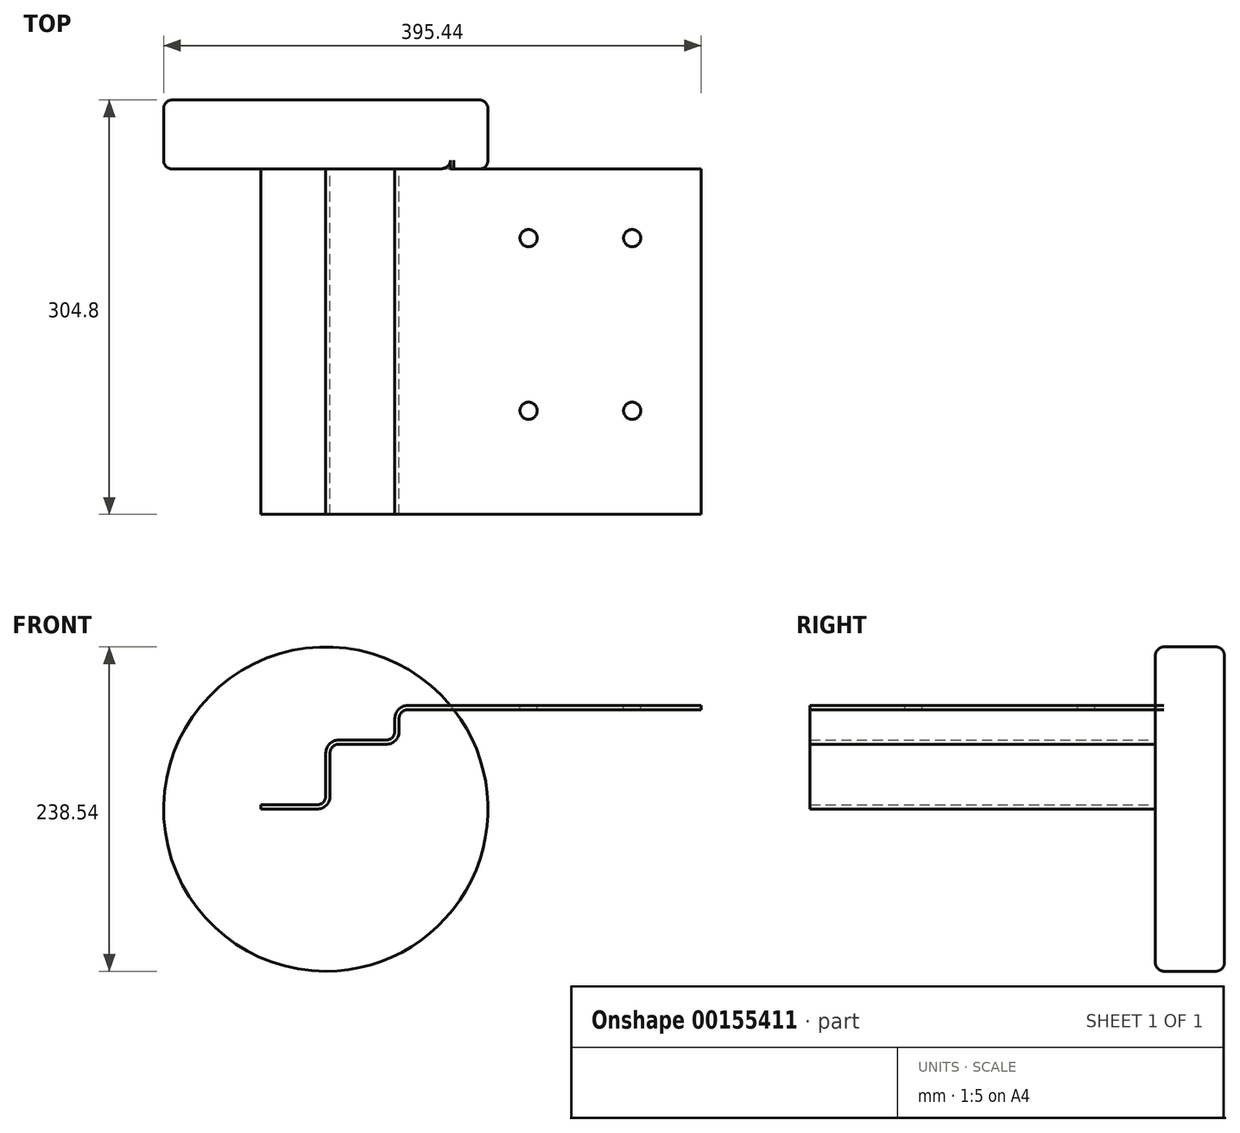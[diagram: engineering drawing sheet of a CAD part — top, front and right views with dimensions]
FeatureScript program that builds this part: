
annotation { "Feature Type Name" : "Feature", "Feature Type Description" : "" }
export const myFeature = defineFeature(function(context is Context, id is Id, definition is map)
    precondition{}
    {
        {
            var Q0;
            Q0=qCreatedBy(makeId("Front.planeOp"),FACE);
            var sketch = newSketch(context, id + "F0", { "sketchPlane" : qUnion([Q0])});
            skLineSegment(sketch, "E0", {"start": v(0, 9.53) * mm, "end": v(0, 41.28) * mm});
            skLineSegment(sketch, "E1", {"start": v(9.52, 50.8) * mm, "end": v(44.45, 50.8) * mm});
            skLineSegment(sketch, "E2", {"start": v(50.8, 57.15) * mm, "end": v(50.8, 66.68) * mm});
            skLineSegment(sketch, "E3", {"start": v(60.33, 76.2) * mm, "end": v(276.17, 76.2) * mm});
            skLineSegment(sketch, "E4.0", {"start": v(60.33, 73.03) * mm, "end": v(276.17, 73.03) * mm});
            skLineSegment(sketch, "E5.0", {"start": v(53.98, 57.15) * mm, "end": v(53.98, 66.68) * mm});
            skLineSegment(sketch, "E6.0", {"start": v(3.18, 9.53) * mm, "end": v(3.18, 41.28) * mm});
            skLineSegment(sketch, "E7", {"start": v(9.52, 47.63) * mm, "end": v(44.45, 47.63) * mm});
            skPoint(sketch, "E8.visualSharp", {"position": v(53.98, 73.03) * mm});
            skArc(sketch, "E8.filletArc", {"start": v(60.33, 73.03) * mm, "mid": v(55.83, 71.17) * mm, "end": v(53.97, 66.68) * mm});
            skArc(sketch, "E9.0", {"start": v(60.33, 76.2) * mm, "mid": v(53.59, 73.41) * mm, "end": v(50.8, 66.68) * mm});
            skPoint(sketch, "E10.visualSharp", {"position": v(50.8, 50.8) * mm});
            skArc(sketch, "E10.filletArc", {"start": v(44.45, 50.8) * mm, "mid": v(48.94, 52.66) * mm, "end": v(50.8, 57.15) * mm});
            skPoint(sketch, "E11.visualSharp", {"position": v(3.18, 47.63) * mm});
            skArc(sketch, "E11.filletArc", {"start": v(9.52, 47.63) * mm, "mid": v(5.03, 45.77) * mm, "end": v(3.17, 41.28) * mm});
            skArc(sketch, "E12.0", {"start": v(44.45, 47.63) * mm, "mid": v(51.19, 50.41) * mm, "end": v(53.98, 57.15) * mm});
            skArc(sketch, "E13.0", {"start": v(9.52, 50.8) * mm, "mid": v(2.79, 48.01) * mm, "end": v(0, 41.28) * mm});
            skPoint(sketch, "E14.orphan", {"position": v(0, 50.8) * mm});
            skLineSegment(sketch, "E15", {"start": v(-47.63, 3.17) * mm, "end": v(-6.35, 3.18) * mm});
            skPoint(sketch, "E16.orphan", {"position": v(0, 0) * mm});
            skLineSegment(sketch, "E17", {"start": v(-47.63, 0) * mm, "end": v(-47.63, 3.17) * mm});
            skPoint(sketch, "E18.visualSharp", {"position": v(0, 3.18) * mm});
            skArc(sketch, "E18.filletArc", {"start": v(-6.35, 3.18) * mm, "mid": v(-1.86, 5.03) * mm, "end": v(0, 9.53) * mm});
            skArc(sketch, "E19.0", {"start": v(-6.35, 0) * mm, "mid": v(0.39, 2.79) * mm, "end": v(3.18, 9.53) * mm});
            skLineSegment(sketch, "E20.trimOffspring", {"start": v(-6.35, 0) * mm, "end": v(-47.63, 0) * mm});
            skLineSegment(sketch, "E21", {"start": v(276.17, 73.03) * mm, "end": v(276.17, 76.2) * mm});
            skSolve(sketch);
        }
        {
            var Q0;
            Q0=makeQuery(id+"F0.imprint","IMPRINT",FACE,{"disambiguationData":[TD([[makeQuery(id+"F0.imprint","IMPRINT",EDGE,{"derivedFrom":sQuery(id+"F0.wireOp",EDGE,"E0")}),-1.0]])]});
            extrude(context, id + "F1", {"entities" : qUnion([Q0]), "depth" : 254 * mm});
        }
        {
            var Q0;
            Q0=qCreatedBy(makeId("Front.planeOp"),FACE);
            var sketch = newSketch(context, id + "F2", { "sketchPlane" : qUnion([Q0])});
            skCircle(sketch, "E22", {"center": v(0, 0) * mm, "radius": 119.27 * mm});
            skSolve(sketch);
        }
        {
            var Q0;
            Q0=makeQuery(id+"F2.imprint","IMPRINT",FACE,{"disambiguationData":[TD([[makeQuery(id+"F2.imprint","IMPRINT",EDGE,{"derivedFrom":sQuery(id+"F2.wireOp",EDGE,"E22")}),1.0]])]});
            extrude(context, id + "F3", {"entities" : qUnion([Q0]), "operationType" : NewBodyOperationType.ADD, "oppositeDirection" : true, "depth" : 50.8 * mm});
        }
        {
            var Q0;
            {var subQ0=sQuery(id+"F2.wireOp",EDGE,"E22");Q0=makeQuery(id+"F3.boolean.opBoolean","SPLIT",EDGE,{"disambiguationData":[topologyDisambiguationEdgeConnected([makeQuery(id+"F3.opExtrude","CAP_FACE",FACE,{"disambiguationData":[OSD([subQ0])],"isStart":true})])],"derivedFrom":makeQuery(id+"F3.opExtrude","CAP_EDGE",EDGE,{"disambiguationData":[OSD([subQ0])],"isStart":true})});}
            var Q1;
            Q1=makeQuery(id+"F3.opExtrude","CAP_EDGE",EDGE,{"disambiguationData":[OSD([sQuery(id+"F2.wireOp",EDGE,"E22")])],"isStart":false});
            fillet(context, id + "F4", {"entities" : qUnion([Q0, Q1]), "radius" : 6.35 * mm, "tangentPropagation" : true, "allowEdgeOverflow" : false});
        }
        {
            var Q0;
            Q0=makeQuery(id+"F1.opExtrude","SWEPT_FACE",FACE,{"disambiguationData":[OSD([sQuery(id+"F0.wireOp",EDGE,"E3")])]});
            var sketch = newSketch(context, id + "F5", { "sketchPlane" : qUnion([Q0])});
            skCircle(sketch, "E23", {"center": v(225.37, -50.8) * mm, "radius": 6.35 * mm});
            skCircle(sketch, "E24", {"center": v(225.37, -177.8) * mm, "radius": 6.35 * mm});
            skCircle(sketch, "E25", {"center": v(149.17, -50.8) * mm, "radius": 6.35 * mm});
            skCircle(sketch, "E26", {"center": v(149.17, -177.8) * mm, "radius": 6.35 * mm});
            skSolve(sketch);
        }
        {
            var Q0;
            Q0=makeQuery(id+"F5.imprint","IMPRINT",FACE,{"disambiguationData":[TD([[makeQuery(id+"F5.imprint","IMPRINT",EDGE,{"derivedFrom":sQuery(id+"F5.wireOp",EDGE,"E23")}),1.0]])]});
            var Q1;
            Q1=makeQuery(id+"F5.imprint","IMPRINT",FACE,{"disambiguationData":[TD([[makeQuery(id+"F5.imprint","IMPRINT",EDGE,{"derivedFrom":sQuery(id+"F5.wireOp",EDGE,"E26")}),1.0]])]});
            var Q2;
            Q2=makeQuery(id+"F5.imprint","IMPRINT",FACE,{"disambiguationData":[TD([[makeQuery(id+"F5.imprint","IMPRINT",EDGE,{"derivedFrom":sQuery(id+"F5.wireOp",EDGE,"E25")}),1.0]])]});
            var Q3;
            Q3=makeQuery(id+"F5.imprint","IMPRINT",FACE,{"disambiguationData":[TD([[makeQuery(id+"F5.imprint","IMPRINT",EDGE,{"derivedFrom":sQuery(id+"F5.wireOp",EDGE,"E24")}),1.0]])]});
            var Q4;
            Q4=sQuery(id+"F5.wireOp",EDGE,"E23");
            var Q5;
            Q5=sQuery(id+"F5.wireOp",EDGE,"E26");
            var Q6;
            Q6=sQuery(id+"F5.wireOp",EDGE,"E24");
            var Q7;
            Q7=sQuery(id+"F5.wireOp",EDGE,"E25");
            extrude(context, id + "F6", {"entities" : qUnion([Q0, Q1, Q2, Q3]), "operationType" : NewBodyOperationType.REMOVE, "surfaceEntities" : qUnion([Q4, Q5, Q6, Q7]), "oppositeDirection" : true, "depth" : 25.4 * mm});
        }
    });
